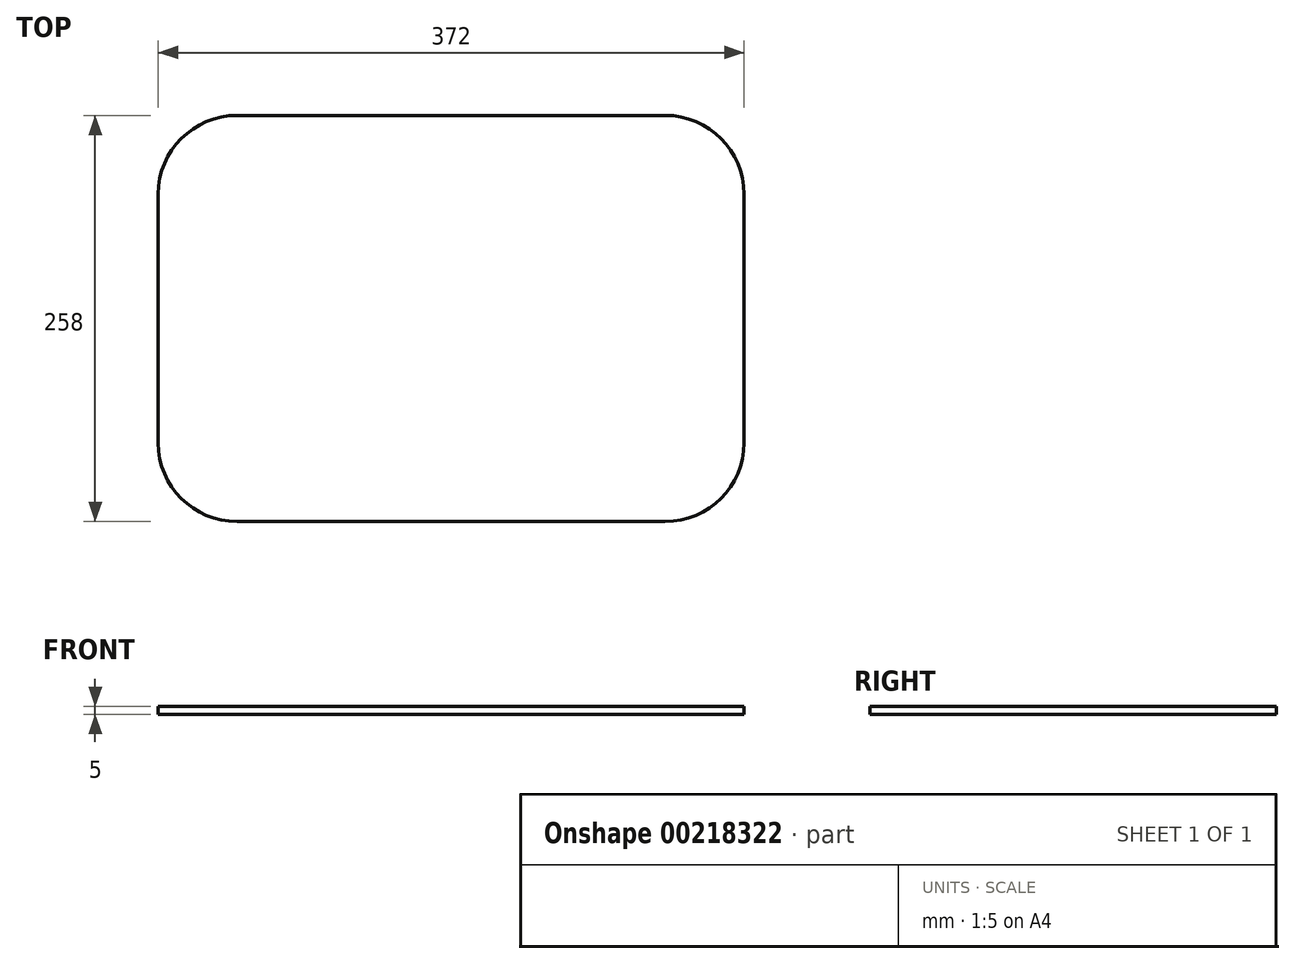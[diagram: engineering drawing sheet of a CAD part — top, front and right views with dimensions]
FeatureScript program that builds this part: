
annotation { "Feature Type Name" : "Feature", "Feature Type Description" : "" }
export const myFeature = defineFeature(function(context is Context, id is Id, definition is map)
    precondition{}
    {
        {
            var Q0;
            Q0=qCreatedBy(makeId("Top.planeOp"),FACE);
            var sketch = newSketch(context, id + "F0", { "sketchPlane" : qUnion([Q0])});
            skLineSegment(sketch, "E0.bottom", {"start": v(-186, 129) * mm, "end": v(186, 129) * mm});
            skLineSegment(sketch, "E0.top", {"start": v(-186, -129) * mm, "end": v(186, -129) * mm});
            skLineSegment(sketch, "E0.left", {"start": v(-186, 129) * mm, "end": v(-186, -129) * mm});
            skLineSegment(sketch, "E0.right", {"start": v(186, 129) * mm, "end": v(186, -129) * mm});
            skPoint(sketch, "E0.middle", {"position": v(0, 0) * mm});
            skSolve(sketch);
        }
        {
            var Q0;
            Q0=makeQuery(id+"F0.imprint","IMPRINT",FACE,{"disambiguationData":[TD([[makeQuery(id+"F0.imprint","IMPRINT",EDGE,{"derivedFrom":sQuery(id+"F0.wireOp",EDGE,"E0.bottom")}),-1.0]])]});
            extrude(context, id + "F1", {"entities" : qUnion([Q0]), "depth" : 5 * mm, "offsetDistance" : 25 * mm});
        }
        {
            var Q0;
            Q0=makeQuery(id+"F1.opExtrude","SWEPT_EDGE",EDGE,{"disambiguationData":[OSD([sQuery(id+"F0.wireOp",EDGE,"E0.top"),sQuery(id+"F0.wireOp",EDGE,"E0.left")])]});
            var Q1;
            Q1=makeQuery(id+"F1.opExtrude","SWEPT_EDGE",EDGE,{"disambiguationData":[OSD([sQuery(id+"F0.wireOp",EDGE,"E0.top"),sQuery(id+"F0.wireOp",EDGE,"E0.right")])]});
            var Q2;
            Q2=makeQuery(id+"F1.opExtrude","SWEPT_EDGE",EDGE,{"disambiguationData":[OSD([sQuery(id+"F0.wireOp",EDGE,"E0.bottom"),sQuery(id+"F0.wireOp",EDGE,"E0.right")])]});
            var Q3;
            Q3=makeQuery(id+"F1.opExtrude","SWEPT_EDGE",EDGE,{"disambiguationData":[OSD([sQuery(id+"F0.wireOp",EDGE,"E0.bottom"),sQuery(id+"F0.wireOp",EDGE,"E0.left")])]});
            fillet(context, id + "F2", {"entities" : qUnion([Q0, Q1, Q2, Q3]), "tangentPropagation" : true, "radius" : 50 * mm, "defaultsChanged" : false, "vertexSettings" : [], "allowEdgeOverflow" : false});
        }
    });
